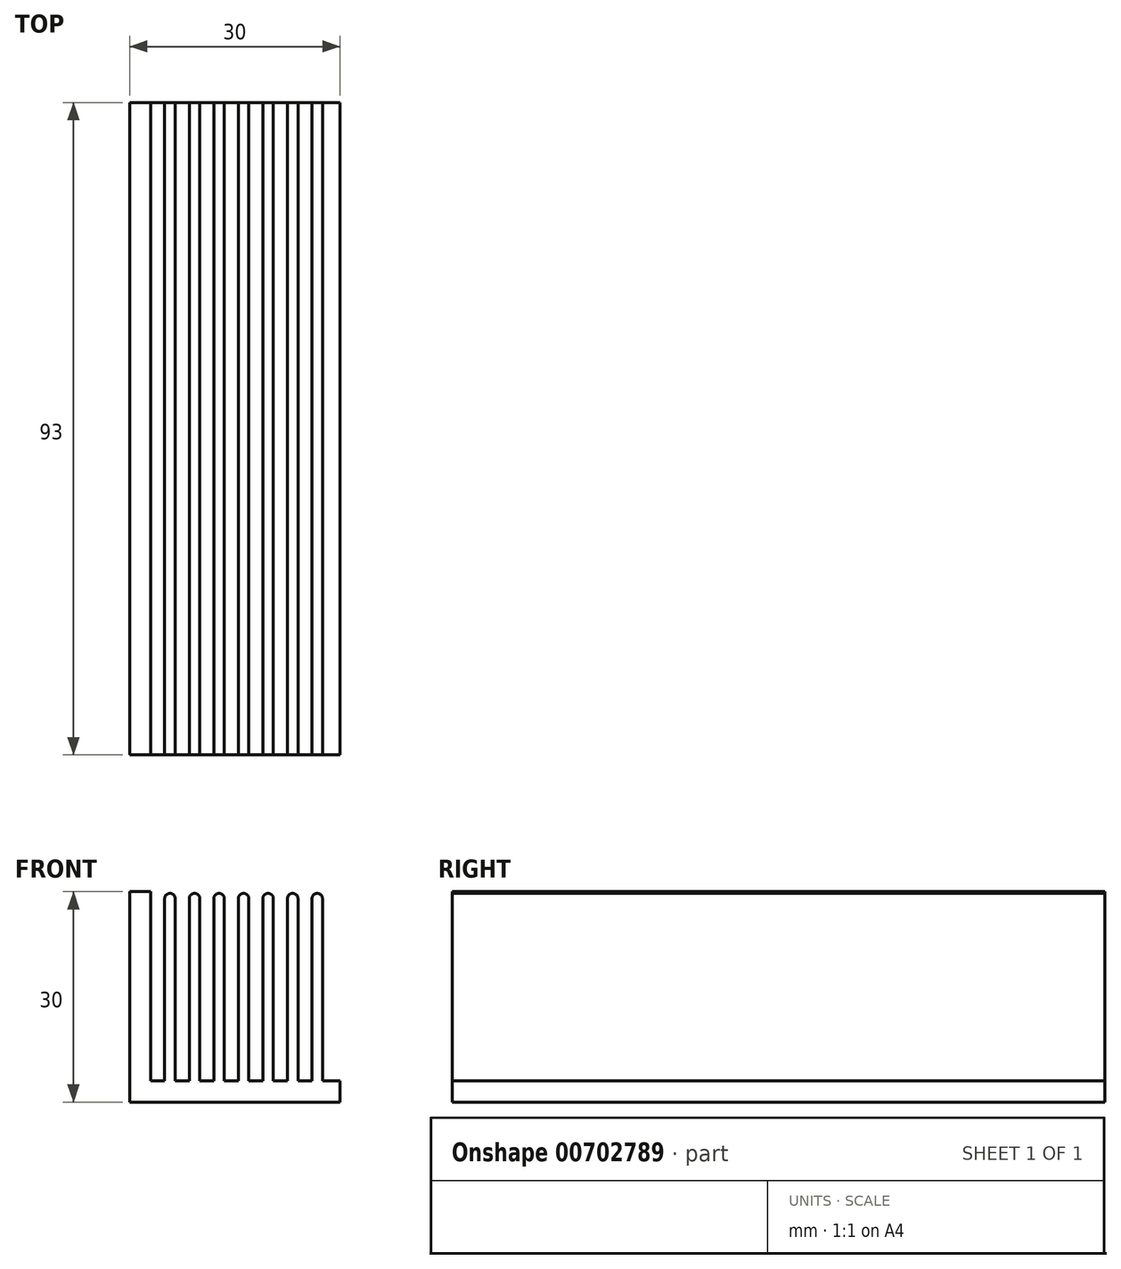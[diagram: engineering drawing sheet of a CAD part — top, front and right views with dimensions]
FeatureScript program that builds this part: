
annotation { "Feature Type Name" : "Feature", "Feature Type Description" : "" }
export const myFeature = defineFeature(function(context is Context, id is Id, definition is map)
    precondition{}
    {
        {
            var Q0;
            Q0=qCreatedBy(makeId("Front.planeOp"),FACE);
            var sketch = newSketch(context, id + "F0", { "sketchPlane" : qUnion([Q0])});
            skLineSegment(sketch, "E0", {"start": v(0, 30) * mm, "end": v(0, 0) * mm});
            skLineSegment(sketch, "E1", {"start": v(0, 0) * mm, "end": v(30, 0) * mm});
            skLineSegment(sketch, "E2", {"start": v(0, 30) * mm, "end": v(3, 30) * mm});
            skLineSegment(sketch, "E3", {"start": v(3, 30) * mm, "end": v(3, 3) * mm});
            skLineSegment(sketch, "E4", {"start": v(3, 3) * mm, "end": v(5, 3) * mm});
            skLineSegment(sketch, "E5", {"start": v(5, 3) * mm, "end": v(5, 29) * mm});
            skLineSegment(sketch, "E6", {"start": v(5, 29) * mm, "end": v(6.5, 29) * mm});
            skLineSegment(sketch, "E7", {"start": v(6.5, 29) * mm, "end": v(6.5, 3) * mm});
            skLineSegment(sketch, "E8", {"start": v(6.5, 3) * mm, "end": v(8.5, 3) * mm});
            skLineSegment(sketch, "E9", {"start": v(8.5, 3) * mm, "end": v(8.5, 29) * mm});
            skLineSegment(sketch, "E10", {"start": v(8.5, 29) * mm, "end": v(10, 29) * mm});
            skLineSegment(sketch, "E11", {"start": v(10, 29) * mm, "end": v(10, 3) * mm});
            skLineSegment(sketch, "E12", {"start": v(10, 3) * mm, "end": v(12, 3) * mm});
            skLineSegment(sketch, "E13", {"start": v(12, 3) * mm, "end": v(12, 29) * mm});
            skLineSegment(sketch, "E14", {"start": v(12, 29) * mm, "end": v(13.5, 29) * mm});
            skLineSegment(sketch, "E15", {"start": v(13.5, 29) * mm, "end": v(13.5, 3) * mm});
            skLineSegment(sketch, "E16", {"start": v(13.5, 3) * mm, "end": v(15.5, 3) * mm});
            skLineSegment(sketch, "E17", {"start": v(15.5, 3) * mm, "end": v(15.5, 29) * mm});
            skLineSegment(sketch, "E18", {"start": v(15.5, 29) * mm, "end": v(17, 29) * mm});
            skLineSegment(sketch, "E19", {"start": v(17, 29) * mm, "end": v(17, 3) * mm});
            skLineSegment(sketch, "E20", {"start": v(17, 3) * mm, "end": v(19, 3) * mm});
            skLineSegment(sketch, "E21", {"start": v(19, 3) * mm, "end": v(19, 29) * mm});
            skLineSegment(sketch, "E22", {"start": v(19, 29) * mm, "end": v(20.5, 29) * mm});
            skLineSegment(sketch, "E23", {"start": v(20.5, 29) * mm, "end": v(20.5, 3) * mm});
            skLineSegment(sketch, "E24", {"start": v(20.5, 3) * mm, "end": v(22.5, 3) * mm});
            skLineSegment(sketch, "E25", {"start": v(22.5, 3) * mm, "end": v(22.5, 29) * mm});
            skLineSegment(sketch, "E26", {"start": v(22.5, 29) * mm, "end": v(24, 29) * mm});
            skLineSegment(sketch, "E27", {"start": v(24, 29) * mm, "end": v(24, 3) * mm});
            skLineSegment(sketch, "E28", {"start": v(24, 3) * mm, "end": v(26, 3) * mm});
            skLineSegment(sketch, "E29", {"start": v(26, 3) * mm, "end": v(26, 29) * mm});
            skLineSegment(sketch, "E30", {"start": v(26, 29) * mm, "end": v(27.5, 29) * mm});
            skLineSegment(sketch, "E31", {"start": v(27.5, 29) * mm, "end": v(27.5, 3) * mm});
            skLineSegment(sketch, "E32", {"start": v(27.5, 3) * mm, "end": v(30, 3) * mm});
            skLineSegment(sketch, "E33", {"start": v(30, 3) * mm, "end": v(30, 0) * mm});
            skArc(sketch, "E34", {"start": v(5, 29) * mm, "mid": v(5.75, 29.75) * mm, "end": v(6.5, 29) * mm});
            skArc(sketch, "E35", {"start": v(8.5, 29) * mm, "mid": v(9.25, 29.75) * mm, "end": v(10, 29) * mm});
            skArc(sketch, "E36", {"start": v(12, 29) * mm, "mid": v(12.75, 29.75) * mm, "end": v(13.5, 29) * mm});
            skArc(sketch, "E37", {"start": v(15.5, 29) * mm, "mid": v(16.25, 29.75) * mm, "end": v(17, 29) * mm});
            skArc(sketch, "E38", {"start": v(19, 29) * mm, "mid": v(19.75, 29.75) * mm, "end": v(20.5, 29) * mm});
            skArc(sketch, "E39", {"start": v(22.5, 29) * mm, "mid": v(23.25, 29.75) * mm, "end": v(24, 29) * mm});
            skArc(sketch, "E40", {"start": v(26, 29) * mm, "mid": v(26.75, 29.75) * mm, "end": v(27.5, 29) * mm});
            skSolve(sketch);
        }
        {
            var Q0;
            Q0 = qSketchRegion(id + "F0", true);
            extrude(context, id + "F1", {"entities" : qUnion([Q0]), "depth" : 93 * mm, "offsetDistance" : 25 * mm});
        }
    });
